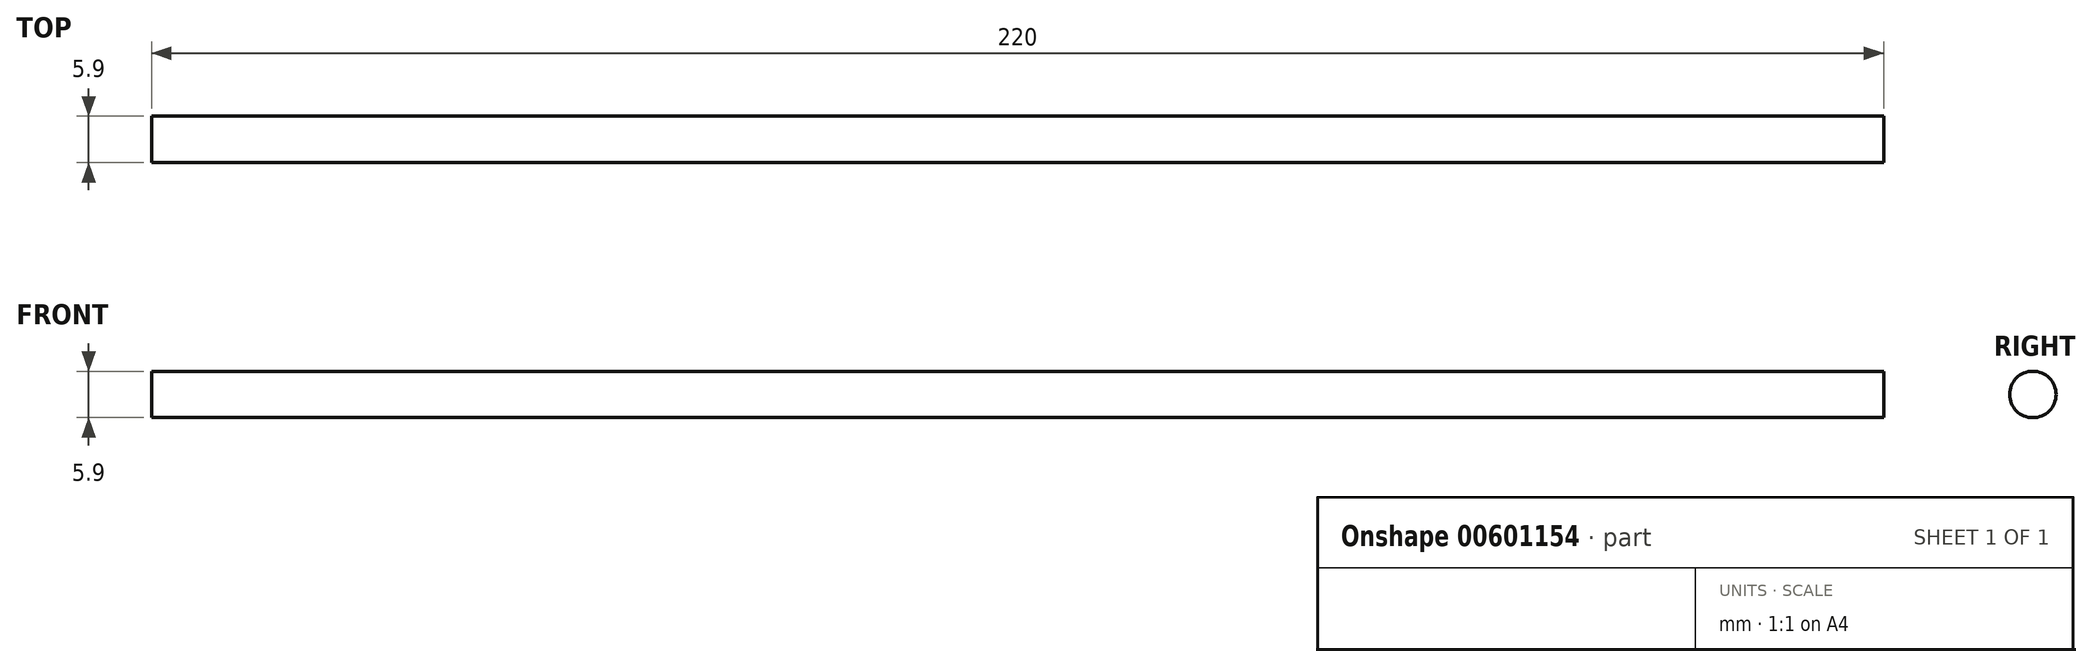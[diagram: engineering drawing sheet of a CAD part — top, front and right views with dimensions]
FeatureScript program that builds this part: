
annotation { "Feature Type Name" : "Feature", "Feature Type Description" : "" }
export const myFeature = defineFeature(function(context is Context, id is Id, definition is map)
    precondition{}
    {
        {
            var Q0;
            Q0=qCreatedBy(makeId("Right.planeOp"),FACE);
            var sketch = newSketch(context, id + "F0", { "sketchPlane" : qUnion([Q0])});
            skCircle(sketch, "E0", {"center": v(0, 0) * mm, "radius": 2.95 * mm});
            skSolve(sketch);
        }
        {
            var Q0;
            Q0=qSketchRegion(id+"F0",true);
            extrude(context, id + "F1", {"entities" : qUnion([Q0]), "depth" : 220 * mm, "offsetDistance" : 25 * mm, "symmetric" : true});
        }
    });
